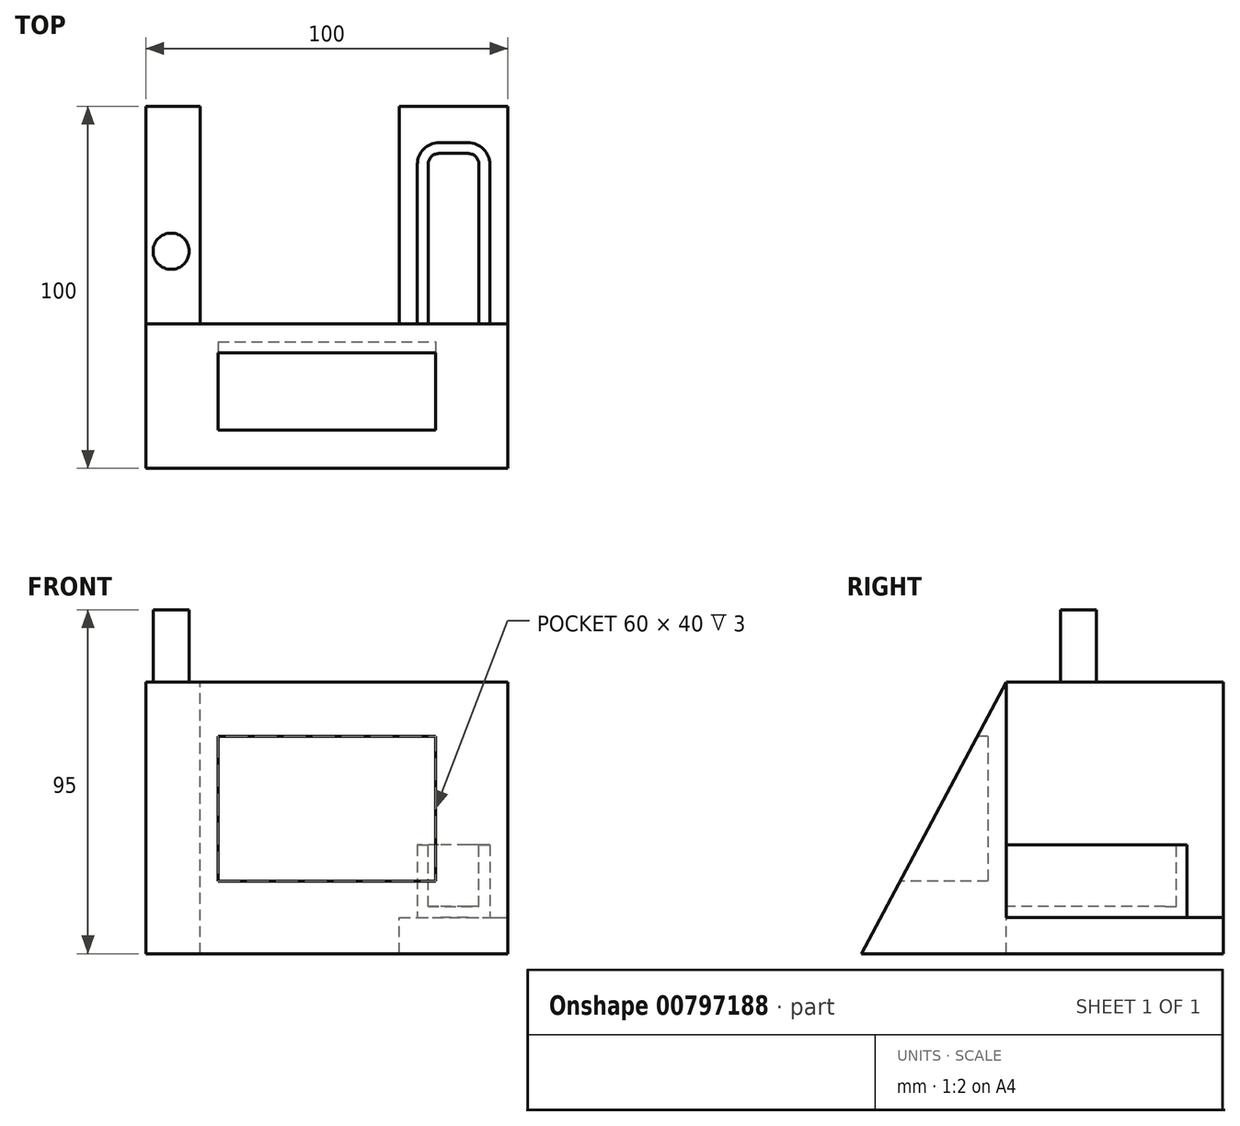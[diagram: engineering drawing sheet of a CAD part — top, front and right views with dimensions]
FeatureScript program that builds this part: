
annotation { "Feature Type Name" : "Feature", "Feature Type Description" : "" }
export const myFeature = defineFeature(function(context is Context, id is Id, definition is map)
    precondition{}
    {
        {
            var Q0;
            Q0=qCreatedBy(makeId("Front.planeOp"),FACE);
            var sketch = newSketch(context, id + "F0", { "sketchPlane" : qUnion([Q0])});
            skLineSegment(sketch, "E0.bottom", {"start": v(0, 0) * mm, "end": v(100, 0) * mm});
            skLineSegment(sketch, "E0.top", {"start": v(0, 75) * mm, "end": v(100, 75) * mm});
            skLineSegment(sketch, "E0.left", {"start": v(0, 0) * mm, "end": v(0, 75) * mm});
            skLineSegment(sketch, "E0.right", {"start": v(100, 0) * mm, "end": v(100, 75) * mm});
            skSolve(sketch);
        }
        {
            var Q0;
            Q0 = qSketchRegion(id + "F0", true);
            extrude(context, id + "F1", {"entities" : qUnion([Q0]), "oppositeDirection" : true, "depth" : 40 * mm, "offsetDistance" : 25 * mm});
        }
        {
            var Q0;
            Q0=makeQuery(id+"F1.opExtrude","SWEPT_FACE",FACE,{"disambiguationData":[OSD([sQuery(id+"F0.wireOp",EDGE,"E0.right")])]});
            var sketch = newSketch(context, id + "F2", { "sketchPlane" : qUnion([Q0])});
            skLineSegment(sketch, "E1", {"start": v(40, 75) * mm, "end": v(0, 0) * mm});
            skLineSegment(sketch, "E2", {"start": v(0, 0) * mm, "end": v(0, 75) * mm});
            skLineSegment(sketch, "E3", {"start": v(0, 75) * mm, "end": v(40, 75) * mm});
            skSolve(sketch);
        }
        {
            var Q0;
            Q0 = qSketchRegion(id + "F2", true);
            extrude(context, id + "F3", {"entities" : qUnion([Q0]), "operationType" : NewBodyOperationType.REMOVE, "endBound" : BoundingType.THROUGH_ALL, "oppositeDirection" : true, "depth" : 25 * mm, "offsetDistance" : 25 * mm});
        }
        {
            var Q0;
            Q0=qCreatedBy(makeId("Front.planeOp"),FACE);
            var sketch = newSketch(context, id + "F4", { "sketchPlane" : qUnion([Q0])});
            skLineSegment(sketch, "E4.bottom", {"start": v(20, 60) * mm, "end": v(80, 60) * mm});
            skLineSegment(sketch, "E4.top", {"start": v(20, 20) * mm, "end": v(80, 20) * mm});
            skLineSegment(sketch, "E4.left", {"start": v(20, 60) * mm, "end": v(20, 20) * mm});
            skLineSegment(sketch, "E4.right", {"start": v(80, 60) * mm, "end": v(80, 20) * mm});
            skSolve(sketch);
        }
        {
            var Q0;
            Q0 = qSketchRegion(id + "F4", true);
            extrude(context, id + "F5", {"entities" : qUnion([Q0]), "operationType" : NewBodyOperationType.REMOVE, "oppositeDirection" : true, "depth" : 35 * mm, "offsetDistance" : 25 * mm});
        }
        {
            var Q0;
            Q0=makeQuery(id+"F1.opExtrude","SWEPT_FACE",FACE,{"disambiguationData":[OSD([sQuery(id+"F0.wireOp",EDGE,"E0.right")])]});
            var sketch = newSketch(context, id + "F6", { "sketchPlane" : qUnion([Q0])});
            skLineSegment(sketch, "E5.bottom", {"start": v(40, 0) * mm, "end": v(100, 0) * mm});
            skLineSegment(sketch, "E5.top", {"start": v(40, 10) * mm, "end": v(100, 10) * mm});
            skLineSegment(sketch, "E5.left", {"start": v(40, 0) * mm, "end": v(40, 10) * mm});
            skLineSegment(sketch, "E5.right", {"start": v(100, 0) * mm, "end": v(100, 10) * mm});
            skSolve(sketch);
        }
        {
            var Q0;
            Q0 = qSketchRegion(id + "F6", true);
            extrude(context, id + "F7", {"entities" : qUnion([Q0]), "operationType" : NewBodyOperationType.ADD, "oppositeDirection" : true, "depth" : 30 * mm, "offsetDistance" : 25 * mm});
        }
        {
            var Q0;
            Q0=makeQuery(id+"F7.opExtrude","SWEPT_FACE",FACE,{"disambiguationData":[OSD([sQuery(id+"F6.wireOp",EDGE,"E5.top")])]});
            var sketch = newSketch(context, id + "F8", { "sketchPlane" : qUnion([Q0])});
            skLineSegment(sketch, "E6.bottom", {"start": v(95, 90) * mm, "end": v(75, 90) * mm});
            skLineSegment(sketch, "E6.top", {"start": v(95, 40) * mm, "end": v(75, 40) * mm});
            skLineSegment(sketch, "E6.left", {"start": v(95, 90) * mm, "end": v(95, 40) * mm});
            skLineSegment(sketch, "E6.right", {"start": v(75, 90) * mm, "end": v(75, 40) * mm});
            skLineSegment(sketch, "E7", {"start": v(85, 90) * mm, "end": v(85, 40) * mm, "construction": true});
            skSolve(sketch);
        }
        {
            var Q0;
            Q0 = qSketchRegion(id + "F8", true);
            extrude(context, id + "F9", {"entities" : qUnion([Q0]), "operationType" : NewBodyOperationType.ADD, "depth" : 20 * mm, "offsetDistance" : 25 * mm});
        }
        {
            var Q0;
            Q0=makeQuery(id+"F9.opExtrude","CAP_FACE",FACE,{"disambiguationData":[OSD([sQuery(id+"F8.wireOp",EDGE,"E6.bottom"),sQuery(id+"F8.wireOp",EDGE,"E6.top"),sQuery(id+"F8.wireOp",EDGE,"E6.left"),sQuery(id+"F8.wireOp",EDGE,"E6.right")])],"isStart":false});
            var sketch = newSketch(context, id + "F10", { "sketchPlane" : qUnion([Q0])});
            skLineSegment(sketch, "E8.0", {"start": v(92, 87) * mm, "end": v(92, 40) * mm});
            skLineSegment(sketch, "E8.1", {"start": v(92, 87) * mm, "end": v(78, 87) * mm});
            skLineSegment(sketch, "E8.2", {"start": v(78, 87) * mm, "end": v(78, 40) * mm});
            skLineSegment(sketch, "E9", {"start": v(92, 40) * mm, "end": v(78, 40) * mm});
            skSolve(sketch);
        }
        {
            var Q0;
            Q0 = qSketchRegion(id + "F10", true);
            extrude(context, id + "F11", {"entities" : qUnion([Q0]), "operationType" : NewBodyOperationType.REMOVE, "oppositeDirection" : true, "depth" : 17 * mm, "offsetDistance" : 25 * mm});
        }
        {
            var Q0;
            Q0=makeQuery(id+"F11.boolean.opBoolean","COPY",EDGE,{"derivedFrom":makeQuery(id+"F11.opExtrude","SWEPT_EDGE",EDGE,{"disambiguationData":[OSD([sQuery(id+"F10.wireOp",EDGE,"E8.1"),sQuery(id+"F10.wireOp",EDGE,"E8.2")])]})});
            var Q1;
            Q1=makeQuery(id+"F11.boolean.opBoolean","COPY",EDGE,{"derivedFrom":makeQuery(id+"F11.opExtrude","SWEPT_EDGE",EDGE,{"disambiguationData":[OSD([sQuery(id+"F10.wireOp",EDGE,"E8.0"),sQuery(id+"F10.wireOp",EDGE,"E8.1")])]})});
            fillet(context, id + "F12", {"entities" : qUnion([Q0, Q1]), "radius" : 3 * mm, "tangentPropagation" : true, "allowEdgeOverflow" : false});
        }
        {
            var Q0;
            Q0=makeQuery(id+"F9.opExtrude","SWEPT_EDGE",EDGE,{"disambiguationData":[OSD([sQuery(id+"F8.wireOp",EDGE,"E6.bottom"),sQuery(id+"F8.wireOp",EDGE,"E6.right")])]});
            var Q1;
            Q1=makeQuery(id+"F9.opExtrude","SWEPT_EDGE",EDGE,{"disambiguationData":[OSD([sQuery(id+"F8.wireOp",EDGE,"E6.bottom"),sQuery(id+"F8.wireOp",EDGE,"E6.left")])]});
            fillet(context, id + "F13", {"entities" : qUnion([Q0, Q1]), "radius" : 6 * mm, "tangentPropagation" : true, "allowEdgeOverflow" : false});
        }
        {
            var Q0;
            Q0=makeQuery(id+"F1.opExtrude","SWEPT_FACE",FACE,{"disambiguationData":[OSD([sQuery(id+"F0.wireOp",EDGE,"E0.left")])]});
            var sketch = newSketch(context, id + "F14", { "sketchPlane" : qUnion([Q0])});
            skLineSegment(sketch, "E10.bottom", {"start": v(-100, 0) * mm, "end": v(-40, 0) * mm});
            skLineSegment(sketch, "E10.top", {"start": v(-100, 75) * mm, "end": v(-40, 75) * mm});
            skLineSegment(sketch, "E10.left", {"start": v(-100, 0) * mm, "end": v(-100, 75) * mm});
            skLineSegment(sketch, "E10.right", {"start": v(-40, 0) * mm, "end": v(-40, 75) * mm});
            skSolve(sketch);
        }
        {
            var Q0;
            Q0 = qSketchRegion(id + "F14", true);
            extrude(context, id + "F15", {"entities" : qUnion([Q0]), "operationType" : NewBodyOperationType.ADD, "oppositeDirection" : true, "depth" : 15 * mm, "offsetDistance" : 25 * mm});
        }
        {
            var Q0;
            Q0=makeQuery(id+"F15.opExtrude","SWEPT_FACE",FACE,{"disambiguationData":[OSD([sQuery(id+"F14.wireOp",EDGE,"E10.top")])]});
            var sketch = newSketch(context, id + "F16", { "sketchPlane" : qUnion([Q0])});
            skCircle(sketch, "E11", {"center": v(7, 60) * mm, "radius": 5 * mm});
            skSolve(sketch);
        }
        {
            var Q0;
            Q0 = qSketchRegion(id + "F16", true);
            extrude(context, id + "F17", {"entities" : qUnion([Q0]), "operationType" : NewBodyOperationType.ADD, "depth" : 20 * mm, "offsetDistance" : 25 * mm});
        }
    });
